# Revit family: Groeninger Fensterantriebe
name_source: partatom
category: Fenster
units: mm (PartAtom-declared; Revit-internal decimal feet)

## family parameters
Basisbauteil = Fläche
Beim Laden mit Abzugskörper schneiden = Nein
Gemeinsam genutzt = Nein
OmniClass-Nummer = 23.30.20.11
OmniClass-Titel = Window Components
Raumberechnungspunkt = Nein

## types (1)
- Fensterantrieb DK-100 (Art. Nr. G1001000)
    Analytische Konstruktion = <Keine Auswahl>
    Anschlagseite = Anschlagseite rechts und links möglich
    Ansteuerung = Taster, Schalter, Totmanntaster
    Bauraum = Bauraum Im unteren Rahmenstück verfügbar
    Befestigung = Ausreichend Material für die Schraubenbefestigung verfügbar
    Beschreibung = Fensterantrieb zum automatisierten Kipp -Öffnen und Kipp -Schließen inklusive Ver- und Entriegeln unter vollem Erhalt der manuellen Bedienung in jeder Fensterstellung und komplett verdeckt liegender Rahmenmontage.
    Einbaulage = Komplett verdeckt liegender, im Profil eingefräster Antrieb, im geschlossenen Zustand nicht sichtbar
    Einschaltdauer (DIN EN 60034-1) = S3  25%; S2  2min
    Endlagen = Automatisiertes Referenzieren der Endlagen
    Erkennung Fensterposition = Im Antrieb integrierte Erkennung der Fensterposition bei automatischer und bei manueller Bedienung
    Falzluft = 12-14mm
    Fensterart = Geeignet für rechteckige Dreh-Kippfenster aus Holz, Kunststoff oder Aluminium
    Firma = Groeninger Antriebstechnik GmbH & Co. KG
Groeninger Antriebstechnik GmbH & Co. KG
    Gebäudeleittechnik / Smart Home = Einbindung in die Gebäudeleittechnik durch potentialfreien Schließerkontakt (digitaler IO)
    Hersteller = Groeninger Antriebstechnik GmbH & Co. KG
    Land = Deutschland
    Lebensdauer = Geprüft mit 20.000 Schaltzyklen (Doppelhub inkl. Verriegelung)
    Lieferumfang = Antrieb
Anschlussleitung 3m PVC
Befestigungsschrauben für Kunststofffenster
Deckel Anschlussbereich inkl. Zugentlastung und Schrauben
Magnet zur Positionserkennung
Aufkleber „Kraftbetätigtes Fenster“
    Manuelle Bedienung = Manuelle Bedienung aller Fensterpositionen (Kippstellung, Drehstellung, Geschlossen) mittels Fenstergriff aus jeder Stellung möglich (Fenstergriff dauerhaft montiert)
    Mitteldichtung = Mitteldichtungssysteme erforderlich
    Modell = Fensterantrieb DK-100 (Art. Nr.: G1001000)
    Mögliche Beschläge = Winkhaus activPilot Ergo, Maco Multi Komfortbeschlag
    Nennstromaufnahme = 0,75 A
    Nutlage = 13mm
    PLZ = 72631
    Reduzierte Geschwindigkeit = Über DIP-Schalter einstellbarer langsamer Modus zur Realisierung leiser Laufgeräusche
    Restwelligkeit = max. 2Vss
    Stadt = Aichtal
    Straße = Alte Str. 9
    Telefon = +49 7127 9606380
    Thermische Eigenschaften definieren durch = Schemaplantypen
    URL = www.fenster-antrieb.de
    Versorgungsspannung durch externes Netzteil = 24V DC
    Vorgabe-Ansicht = 1219 mm
    Website = www.fenster-antrieb.de
    Zusatzkomponenten = keine Zusatzkomponenten wie z.B. Konsolen zur Antriebsbefestigung oder Elemente zum Übertragen der Antriebskraft erforderlich
    max. Flügelgewicht = 60 kg
    Öffnungs- / Schließzeit = ca. 28s im normalen Modus und ca. 35s im langsamen Modus
    Öffnungs- und Schließkraft = 800N über die Riegelstange
    Öffnungsweite = Kipp-Öffnungsweite zwischen 100 mm und 130 mm in Abhängigkeit des verwendeten Beschlags
